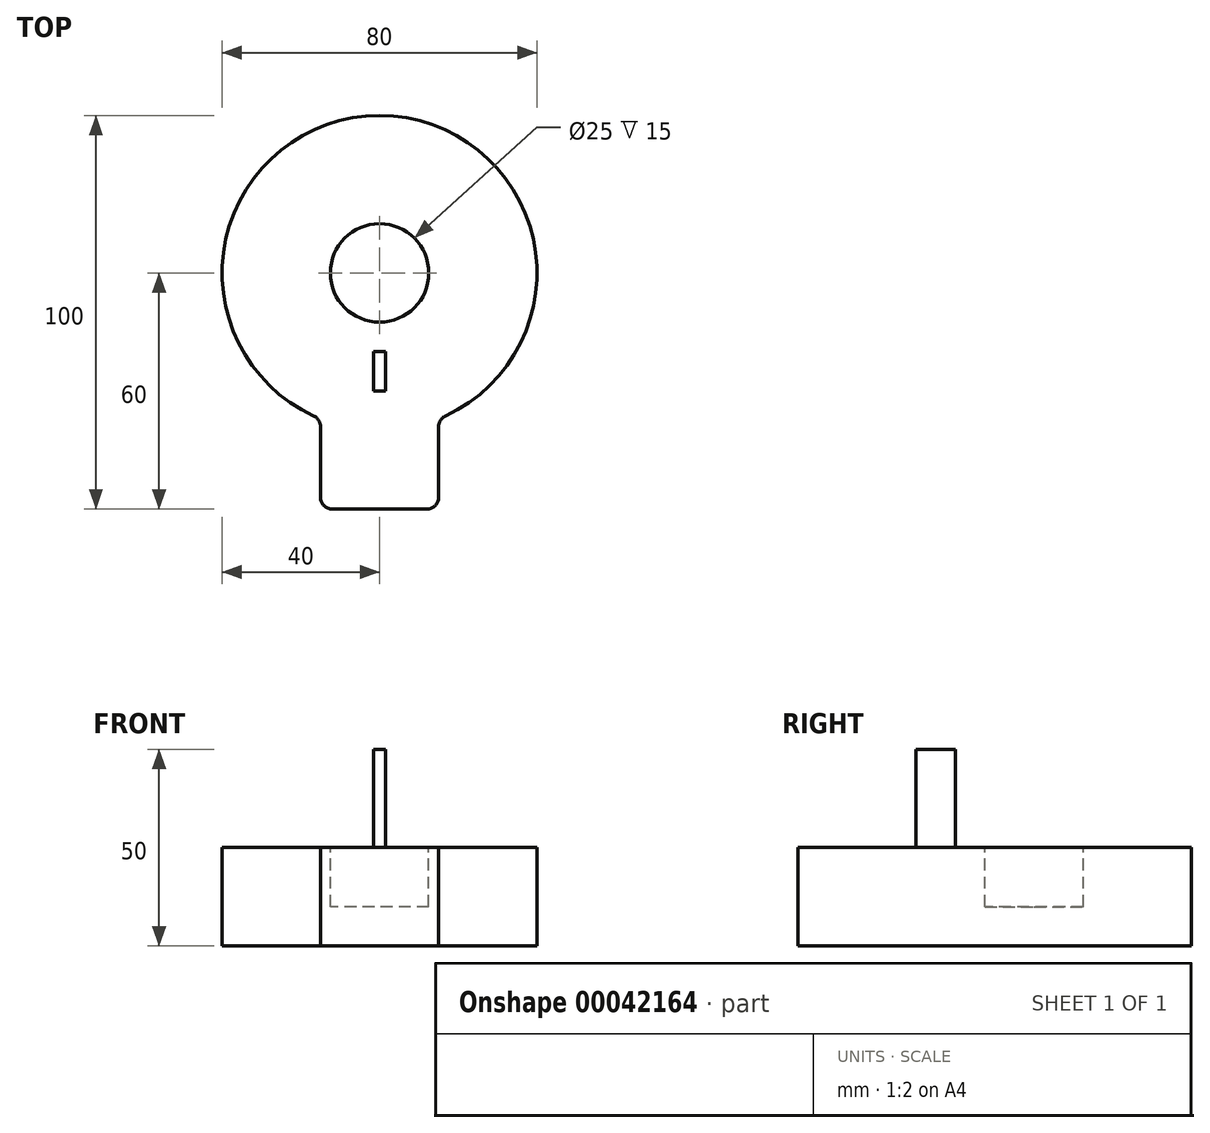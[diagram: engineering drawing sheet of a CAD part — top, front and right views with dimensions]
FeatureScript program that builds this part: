
annotation { "Feature Type Name" : "Feature", "Feature Type Description" : "" }
export const myFeature = defineFeature(function(context is Context, id is Id, definition is map)
    precondition{}
    {
        {
            var Q0;
            Q0=qCreatedBy(makeId("Top.planeOp"),FACE);
            var sketch = newSketch(context, id + "F0", { "sketchPlane" : qUnion([Q0])});
            skArc(sketch, "E0", {"start": v(16.74, -36.33) * mm, "mid": v(0, 40) * mm, "end": v(-16.74, -36.33) * mm});
            skLineSegment(sketch, "E1", {"start": v(-15, -39.05) * mm, "end": v(-15, -57) * mm});
            skLineSegment(sketch, "E2", {"start": v(-12, -60) * mm, "end": v(12, -60) * mm});
            skLineSegment(sketch, "E3", {"start": v(15, -57) * mm, "end": v(15, -39.05) * mm});
            skPoint(sketch, "E4.orphan", {"position": v(15, 0) * mm});
            skLineSegment(sketch, "E5", {"start": v(0, 0) * mm, "end": v(0, -70) * mm, "construction": true});
            skPoint(sketch, "E6.visualSharp", {"position": v(-15, -60) * mm});
            skArc(sketch, "E6.filletArc", {"start": v(-15, -57) * mm, "mid": v(-14.12, -59.12) * mm, "end": v(-12, -60) * mm});
            skPoint(sketch, "E7.visualSharp", {"position": v(15, -60) * mm});
            skArc(sketch, "E7.filletArc", {"start": v(12, -60) * mm, "mid": v(14.12, -59.12) * mm, "end": v(15, -57) * mm});
            skPoint(sketch, "E8.visualSharp", {"position": v(-15, -37.08) * mm});
            skArc(sketch, "E8.filletArc", {"start": v(-15, -39.05) * mm, "mid": v(-15.47, -37.43) * mm, "end": v(-16.74, -36.33) * mm});
            skPoint(sketch, "E9.visualSharp", {"position": v(15, -37.08) * mm});
            skArc(sketch, "E9.filletArc", {"start": v(16.74, -36.33) * mm, "mid": v(15.47, -37.43) * mm, "end": v(15, -39.05) * mm});
            skSolve(sketch);
        }
        {
            var Q0;
            Q0=makeQuery(id+"F0.imprint","IMPRINT",FACE,{"disambiguationData":[TD([[makeQuery(id+"F0.imprint","IMPRINT",EDGE,{"derivedFrom":sQuery(id+"F0.wireOp",EDGE,"E0")}),1.0]])]});
            extrude(context, id + "F1", {"entities" : qUnion([Q0]), "depth" : 25 * mm});
        }
        {
            var Q0;
            Q0=makeQuery(id+"F1.opExtrude","CAP_FACE",FACE,{"disambiguationData":[OSD([sQuery(id+"F0.wireOp",EDGE,"E0"),sQuery(id+"F0.wireOp",EDGE,"E1"),sQuery(id+"F0.wireOp",EDGE,"E2"),sQuery(id+"F0.wireOp",EDGE,"E3"),sQuery(id+"F0.wireOp",EDGE,"E6.filletArc"),sQuery(id+"F0.wireOp",EDGE,"E7.filletArc"),sQuery(id+"F0.wireOp",EDGE,"E8.filletArc"),sQuery(id+"F0.wireOp",EDGE,"E9.filletArc")])],"isStart":false});
            var sketch = newSketch(context, id + "F2", { "sketchPlane" : qUnion([Q0])});
            skCircle(sketch, "E10", {"center": v(0, 0) * mm, "radius": 12.5 * mm});
            skSolve(sketch);
        }
        {
            var Q0;
            Q0 = qSketchRegion(id + "F2", true);
            extrude(context, id + "F3", {"entities" : qUnion([Q0]), "operationType" : NewBodyOperationType.REMOVE, "oppositeDirection" : true, "depth" : 15 * mm});
        }
        {
            var Q0;
            Q0=qCreatedBy(makeId("Right.planeOp"),FACE);
            var sketch = newSketch(context, id + "F4", { "sketchPlane" : qUnion([Q0])});
            skLineSegment(sketch, "E11.bottom", {"start": v(-30, 25) * mm, "end": v(-20, 25) * mm});
            skLineSegment(sketch, "E11.top", {"start": v(-30, 50) * mm, "end": v(-20, 50) * mm});
            skLineSegment(sketch, "E11.left", {"start": v(-30, 25) * mm, "end": v(-30, 50) * mm});
            skLineSegment(sketch, "E11.right", {"start": v(-20, 25) * mm, "end": v(-20, 50) * mm});
            skLineSegment(sketch, "E12", {"start": v(0, -8.39) * mm, "end": v(0, 32.08) * mm, "construction": true});
            skSolve(sketch);
        }
        {
            var Q0;
            Q0 = qSketchRegion(id + "F4", true);
            extrude(context, id + "F5", {"entities" : qUnion([Q0]), "operationType" : NewBodyOperationType.ADD, "endBound" : BoundingType.SYMMETRIC, "depth" : 3 * mm});
        }
    });
